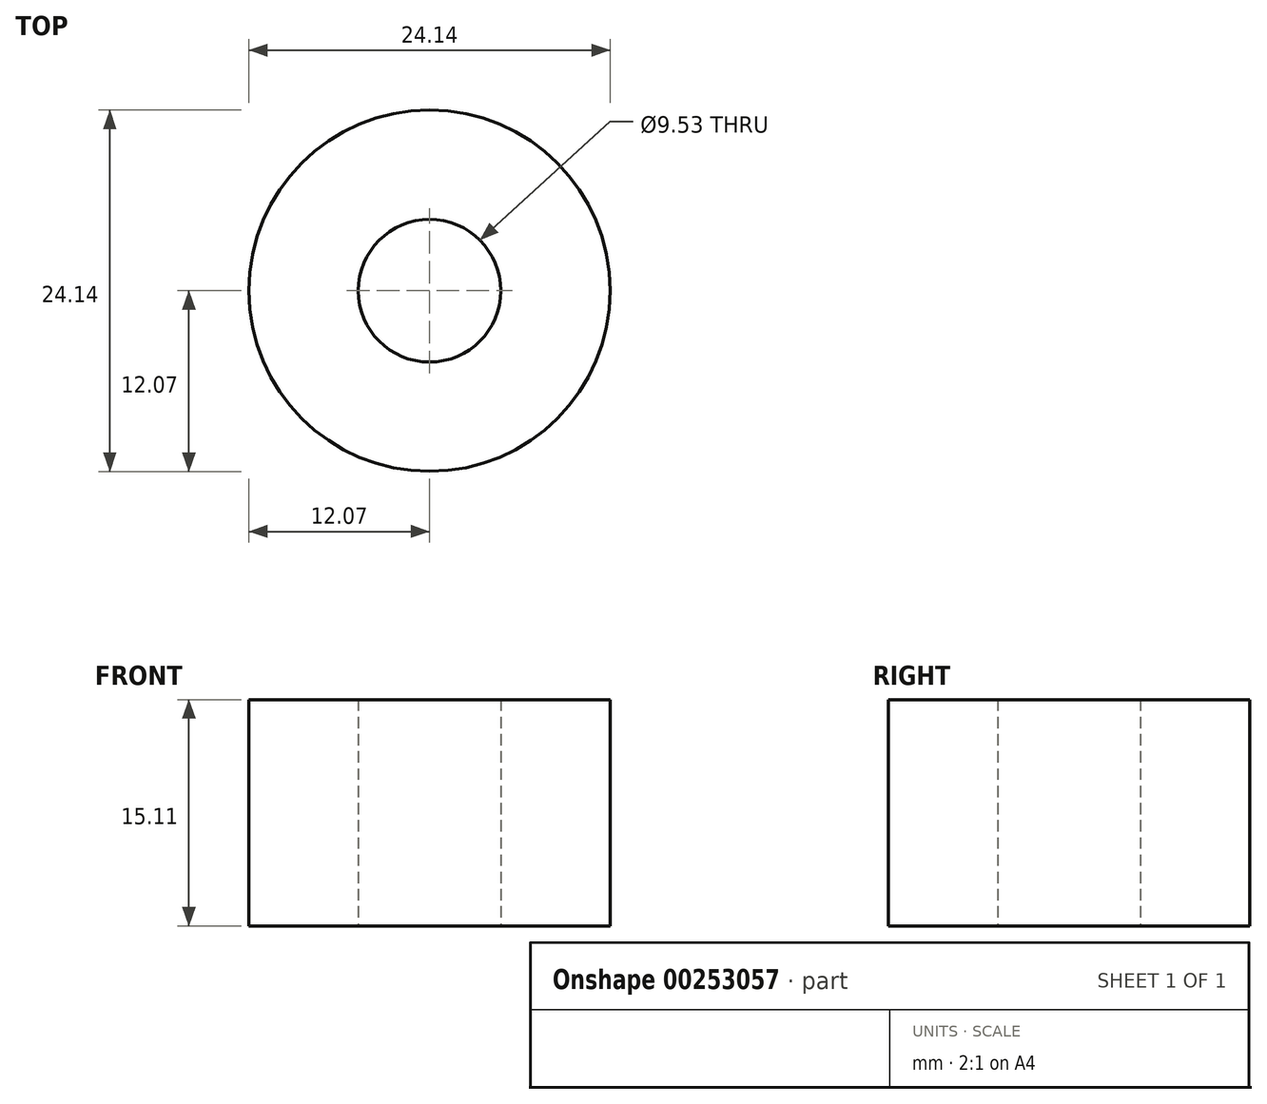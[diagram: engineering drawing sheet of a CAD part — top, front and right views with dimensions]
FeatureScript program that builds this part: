
annotation { "Feature Type Name" : "Feature", "Feature Type Description" : "" }
export const myFeature = defineFeature(function(context is Context, id is Id, definition is map)
    precondition{}
    {
        {
            var Q0;
            Q0=qCreatedBy(makeId("Top.planeOp"),FACE);
            var sketch = newSketch(context, id + "F0", { "sketchPlane" : qUnion([Q0])});
            skCircle(sketch, "E0", {"center": v(0, 0) * mm, "radius": 12.07 * mm});
            skCircle(sketch, "E1", {"center": v(0, 0) * mm, "radius": 4.76 * mm});
            skSolve(sketch);
        }
        {
            var Q0;
            Q0 = qSketchRegion(id + "F0", true);
            extrude(context, id + "F1", {"entities" : qUnion([Q0]), "depth" : 15.1 * mm});
        }
    });
